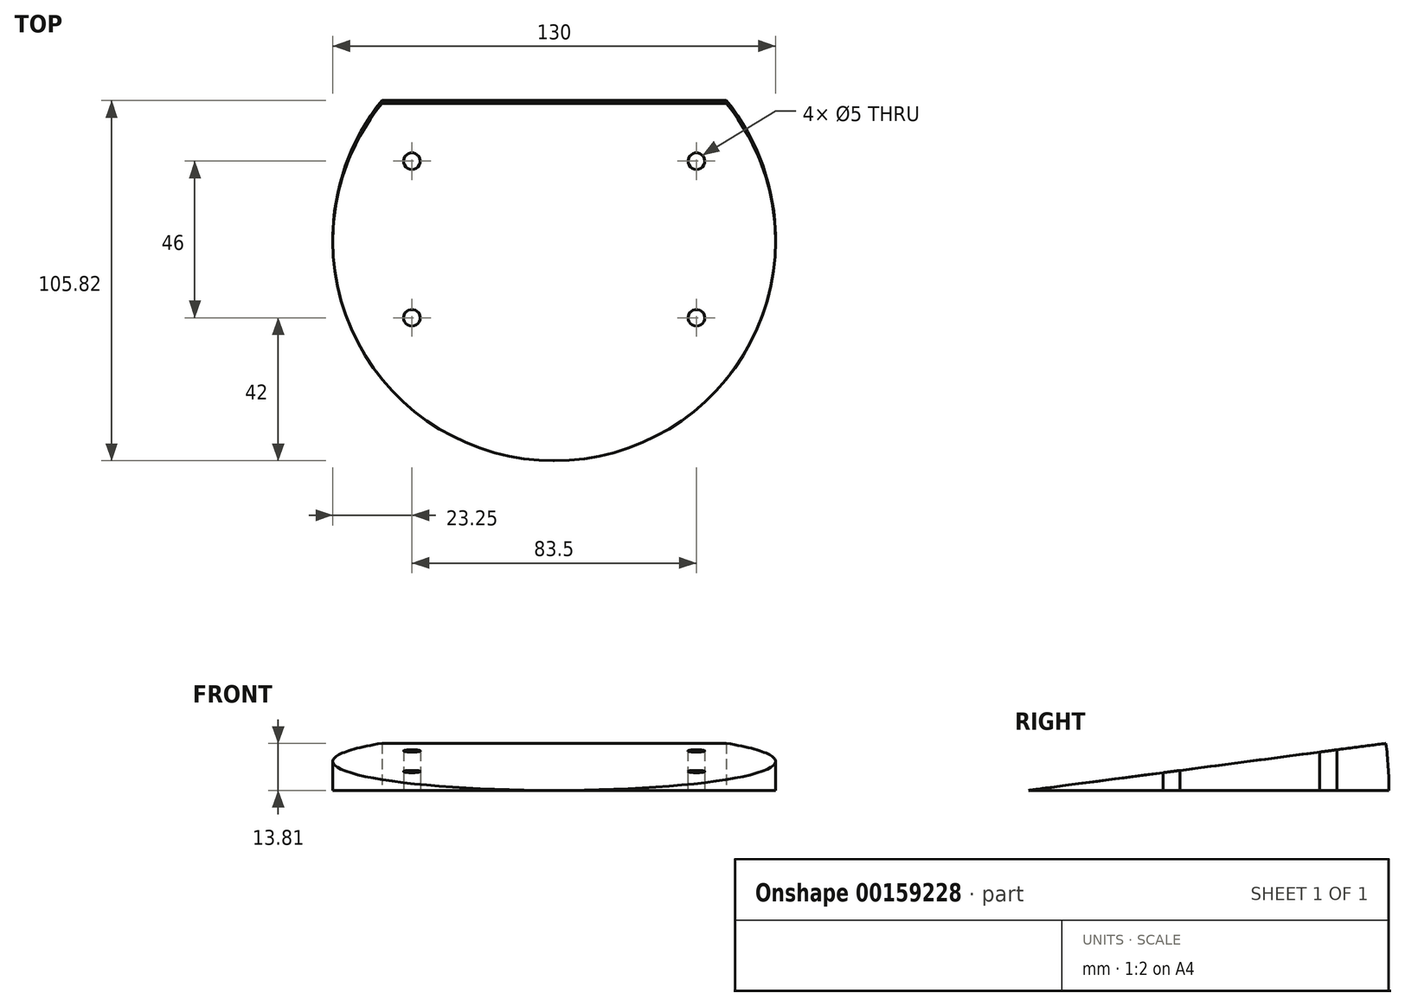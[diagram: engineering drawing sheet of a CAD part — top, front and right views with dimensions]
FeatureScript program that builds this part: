
annotation { "Feature Type Name" : "Feature", "Feature Type Description" : "" }
export const myFeature = defineFeature(function(context is Context, id is Id, definition is map)
    precondition{}
    {
        {
            var Q0;
            Q0=qCreatedBy(makeId("Top.planeOp"),FACE);
            var sketch = newSketch(context, id + "F0", { "sketchPlane" : qUnion([Q0])});
            skCircle(sketch, "E0", {"center": v(0, 0) * mm, "radius": 65 * mm});
            skLineSegment(sketch, "E1.bottom", {"start": v(41.75, -23) * mm, "end": v(-41.75, -23) * mm});
            skLineSegment(sketch, "E1.top", {"start": v(41.75, 23) * mm, "end": v(-41.75, 23) * mm});
            skLineSegment(sketch, "E1.left", {"start": v(41.75, -23) * mm, "end": v(41.75, 23) * mm});
            skLineSegment(sketch, "E1.right", {"start": v(-41.75, -23) * mm, "end": v(-41.75, 23) * mm});
            skCircle(sketch, "E2", {"center": v(-41.75, 23) * mm, "radius": 2.5 * mm});
            skCircle(sketch, "E3.0.1.0", {"center": v(-41.75, -23) * mm, "radius": 2.5 * mm});
            skCircle(sketch, "E3.1.0.0", {"center": v(41.75, 23) * mm, "radius": 2.5 * mm});
            skCircle(sketch, "E3.1.1.0", {"center": v(41.75, -23) * mm, "radius": 2.5 * mm});
            skLineSegment(sketch, "E3.direction1", {"start": v(-41.75, 23) * mm, "end": v(41.75, 23) * mm, "construction": true});
            skLineSegment(sketch, "E3.direction2", {"start": v(-41.75, 23) * mm, "end": v(-41.75, -23) * mm, "construction": true});
            skLineSegment(sketch, "E4", {"start": v(0, -65) * mm, "end": v(66.65, -65) * mm});
            skLineSegment(sketch, "E5", {"start": v(50.59, 40.82) * mm, "end": v(-50.59, 40.82) * mm});
            skSolve(sketch);
        }
        {
            var Q0;
            Q0=makeQuery(id+"F0.imprint","IMPRINT",FACE,{"disambiguationData":[TD([[makeQuery(id+"F0.imprint","IMPRINT",EDGE,{"derivedFrom":sQuery(id+"F0.wireOp",EDGE,"E0")}),1.0]])]});
            var Q1;
            {var subQ5=sQuery(id+"F0.wireOp",EDGE,"E3.1.1.0");var subQ13=sQuery(id+"F0.wireOp",EDGE,"E1.bottom");var subQ14=makeQuery(id+"F0.imprint","INTERSECT",VERTEX,{"derivedFrom":[subQ13,subQ5]});Q1=makeQuery(id+"F0.imprint","IMPRINT",FACE,{"disambiguationData":[TD([[makeQuery(id+"F0.imprint","IMPRINT",EDGE,{"disambiguationData":[TD([[subQ14,-1.0]])],"derivedFrom":subQ13}),-1.0]])]});}
            var Q2;
            {var subQ0=sQuery(id+"F0.wireOp",EDGE,"E1.right");var subQ1=sQuery(id+"F0.wireOp",EDGE,"E1.bottom");var subQ2=makeQuery(id+"F0.imprint","INTERSECT",VERTEX,{"derivedFrom":[subQ1,subQ0]});Q2=makeQuery(id+"F0.imprint","IMPRINT",FACE,{"disambiguationData":[TD([[makeQuery(id+"F0.imprint","IMPRINT",EDGE,{"disambiguationData":[TD([[subQ2,1.0]])],"derivedFrom":subQ1}),1.0]])]});}
            var Q3;
            {var subQ0=sQuery(id+"F0.wireOp",EDGE,"E1.left");var subQ1=sQuery(id+"F0.wireOp",EDGE,"E1.bottom");var subQ2=makeQuery(id+"F0.imprint","INTERSECT",VERTEX,{"derivedFrom":[subQ1,subQ0]});Q3=makeQuery(id+"F0.imprint","IMPRINT",FACE,{"disambiguationData":[TD([[makeQuery(id+"F0.imprint","IMPRINT",EDGE,{"disambiguationData":[TD([[subQ2,-1.0]])],"derivedFrom":subQ1}),1.0]])]});}
            var Q4;
            {var subQ0=sQuery(id+"F0.wireOp",EDGE,"E1.left");var subQ1=sQuery(id+"F0.wireOp",EDGE,"E1.top");var subQ2=makeQuery(id+"F0.imprint","INTERSECT",VERTEX,{"derivedFrom":[subQ1,subQ0]});Q4=makeQuery(id+"F0.imprint","IMPRINT",FACE,{"disambiguationData":[TD([[makeQuery(id+"F0.imprint","IMPRINT",EDGE,{"disambiguationData":[TD([[subQ2,-1.0]])],"derivedFrom":subQ1}),1.0]])]});}
            var Q5;
            {var subQ0=sQuery(id+"F0.wireOp",EDGE,"E1.right");var subQ1=sQuery(id+"F0.wireOp",EDGE,"E1.top");var subQ2=makeQuery(id+"F0.imprint","INTERSECT",VERTEX,{"derivedFrom":[subQ1,subQ0]});Q5=makeQuery(id+"F0.imprint","IMPRINT",FACE,{"disambiguationData":[TD([[makeQuery(id+"F0.imprint","IMPRINT",EDGE,{"disambiguationData":[TD([[subQ2,1.0]])],"derivedFrom":subQ1}),1.0]])]});}
            var Q6;
            {var subQ0=sQuery(id+"F0.wireOp",EDGE,"E1.right");var subQ1=sQuery(id+"F0.wireOp",EDGE,"E1.top");var subQ2=makeQuery(id+"F0.imprint","INTERSECT",VERTEX,{"derivedFrom":[subQ1,subQ0]});Q6=makeQuery(id+"F0.imprint","IMPRINT",FACE,{"disambiguationData":[TD([[makeQuery(id+"F0.imprint","IMPRINT",EDGE,{"disambiguationData":[TD([[subQ2,1.0]])],"derivedFrom":subQ1}),-1.0]])]});}
            var Q7;
            {var subQ0=sQuery(id+"F0.wireOp",EDGE,"E1.right");var subQ1=sQuery(id+"F0.wireOp",EDGE,"E1.bottom");var subQ2=makeQuery(id+"F0.imprint","INTERSECT",VERTEX,{"derivedFrom":[subQ1,subQ0]});Q7=makeQuery(id+"F0.imprint","IMPRINT",FACE,{"disambiguationData":[TD([[makeQuery(id+"F0.imprint","IMPRINT",EDGE,{"disambiguationData":[TD([[subQ2,1.0]])],"derivedFrom":subQ1}),-1.0]])]});}
            var Q8;
            {var subQ0=sQuery(id+"F0.wireOp",EDGE,"E1.left");var subQ1=sQuery(id+"F0.wireOp",EDGE,"E1.bottom");var subQ2=makeQuery(id+"F0.imprint","INTERSECT",VERTEX,{"derivedFrom":[subQ1,subQ0]});Q8=makeQuery(id+"F0.imprint","IMPRINT",FACE,{"disambiguationData":[TD([[makeQuery(id+"F0.imprint","IMPRINT",EDGE,{"disambiguationData":[TD([[subQ2,-1.0]])],"derivedFrom":subQ1}),-1.0]])]});}
            var Q9;
            {var subQ0=sQuery(id+"F0.wireOp",EDGE,"E1.left");var subQ1=sQuery(id+"F0.wireOp",EDGE,"E1.top");var subQ2=makeQuery(id+"F0.imprint","INTERSECT",VERTEX,{"derivedFrom":[subQ1,subQ0]});Q9=makeQuery(id+"F0.imprint","IMPRINT",FACE,{"disambiguationData":[TD([[makeQuery(id+"F0.imprint","IMPRINT",EDGE,{"disambiguationData":[TD([[subQ2,-1.0]])],"derivedFrom":subQ1}),-1.0]])]});}
            var Q10;
            {var subQ0=sQuery(id+"F0.wireOp",EDGE,"61955078-7550-41af-9b48-997e45a96210.0.1.0");var subQ1=sQuery(id+"F0.wireOp",EDGE,"E1.bottom");var subQ2=makeQuery(id+"F0.imprint","INTERSECT",VERTEX,{"derivedFrom":[subQ1,subQ0]});Q10=makeQuery(id+"F0.imprint","IMPRINT",FACE,{"disambiguationData":[TD([[makeQuery(id+"F0.imprint","IMPRINT",EDGE,{"disambiguationData":[TD([[subQ2,-1.0]])],"derivedFrom":subQ1}),-1.0]])]});}
            var Q11;
            {var subQ0=sQuery(id+"F0.wireOp",EDGE,"61955078-7550-41af-9b48-997e45a96210.0.1.0");var subQ1=sQuery(id+"F0.wireOp",EDGE,"E1.bottom");var subQ2=makeQuery(id+"F0.imprint","INTERSECT",VERTEX,{"derivedFrom":[subQ1,subQ0]});Q11=makeQuery(id+"F0.imprint","IMPRINT",FACE,{"disambiguationData":[TD([[makeQuery(id+"F0.imprint","IMPRINT",EDGE,{"disambiguationData":[TD([[subQ2,-1.0]])],"derivedFrom":subQ1}),1.0]])]});}
            var Q12;
            {var subQ0=sQuery(id+"F0.wireOp",EDGE,"61955078-7550-41af-9b48-997e45a96210.1.1.0");var subQ6=sQuery(id+"F0.wireOp",EDGE,"E1.bottom");var subQ15=makeQuery(id+"F0.imprint","INTERSECT",VERTEX,{"derivedFrom":[subQ6,subQ0]});Q12=makeQuery(id+"F0.imprint","IMPRINT",FACE,{"disambiguationData":[TD([[makeQuery(id+"F0.imprint","IMPRINT",EDGE,{"disambiguationData":[TD([[subQ15,-1.0]])],"derivedFrom":subQ6}),-1.0]])]});}
            var Q13;
            {var subQ0=sQuery(id+"F0.wireOp",EDGE,"YlbtFvMg-89HG-Mmdf-bFzC-3wuNxcR9Jd2W");var subQ1=sQuery(id+"F0.wireOp",EDGE,"E1.top");var subQ2=makeQuery(id+"F0.imprint","INTERSECT",VERTEX,{"derivedFrom":[subQ1,subQ0]});Q13=makeQuery(id+"F0.imprint","IMPRINT",FACE,{"disambiguationData":[TD([[makeQuery(id+"F0.imprint","IMPRINT",EDGE,{"disambiguationData":[TD([[subQ2,-1.0]])],"derivedFrom":subQ1}),1.0]])]});}
            var Q14;
            {var subQ0=sQuery(id+"F0.wireOp",EDGE,"YlbtFvMg-89HG-Mmdf-bFzC-3wuNxcR9Jd2W");var subQ1=sQuery(id+"F0.wireOp",EDGE,"E1.top");var subQ2=makeQuery(id+"F0.imprint","INTERSECT",VERTEX,{"derivedFrom":[subQ1,subQ0]});Q14=makeQuery(id+"F0.imprint","IMPRINT",FACE,{"disambiguationData":[TD([[makeQuery(id+"F0.imprint","IMPRINT",EDGE,{"disambiguationData":[TD([[subQ2,-1.0]])],"derivedFrom":subQ1}),-1.0]])]});}
            var Q15;
            {var subQ0=sQuery(id+"F0.wireOp",EDGE,"E3.1.0.0");var subQ1=sQuery(id+"F0.wireOp",EDGE,"E1.top");var subQ2=makeQuery(id+"F0.imprint","INTERSECT",VERTEX,{"derivedFrom":[subQ1,subQ0]});Q15=makeQuery(id+"F0.imprint","IMPRINT",FACE,{"disambiguationData":[TD([[makeQuery(id+"F0.imprint","IMPRINT",EDGE,{"disambiguationData":[TD([[subQ2,-1.0]])],"derivedFrom":subQ1}),1.0]])]});}
            var Q16;
            {var subQ0=sQuery(id+"F0.wireOp",EDGE,"E3.1.0.0");var subQ1=sQuery(id+"F0.wireOp",EDGE,"E1.top");var subQ2=makeQuery(id+"F0.imprint","INTERSECT",VERTEX,{"derivedFrom":[subQ1,subQ0]});Q16=makeQuery(id+"F0.imprint","IMPRINT",FACE,{"disambiguationData":[TD([[makeQuery(id+"F0.imprint","IMPRINT",EDGE,{"disambiguationData":[TD([[subQ2,-1.0]])],"derivedFrom":subQ1}),-1.0]])]});}
            var Q17;
            {var subQ0=sQuery(id+"F0.wireOp",EDGE,"E3.1.1.0");var subQ1=sQuery(id+"F0.wireOp",EDGE,"E1.bottom");var subQ2=makeQuery(id+"F0.imprint","INTERSECT",VERTEX,{"derivedFrom":[subQ1,subQ0]});Q17=makeQuery(id+"F0.imprint","IMPRINT",FACE,{"disambiguationData":[TD([[makeQuery(id+"F0.imprint","IMPRINT",EDGE,{"disambiguationData":[TD([[subQ2,-1.0]])],"derivedFrom":subQ1}),1.0]])]});}
            var Q18;
            {var subQ0=sQuery(id+"F0.wireOp",EDGE,"61955078-7550-41af-9b48-997e45a96210.1.0.0");var subQ1=sQuery(id+"F0.wireOp",EDGE,"E1.top");var subQ2=makeQuery(id+"F0.imprint","INTERSECT",VERTEX,{"derivedFrom":[subQ1,subQ0]});Q18=makeQuery(id+"F0.imprint","IMPRINT",FACE,{"disambiguationData":[TD([[makeQuery(id+"F0.imprint","IMPRINT",EDGE,{"disambiguationData":[TD([[subQ2,-1.0]])],"derivedFrom":subQ1}),-1.0]])]});}
            var Q19;
            {var subQ0=sQuery(id+"F0.wireOp",EDGE,"6T6w9VIw-9FXo-ThLn-9DWL-4RXQOPPDTeL3.top");var subQ1=sQuery(id+"F0.wireOp",EDGE,"61955078-7550-41af-9b48-997e45a96210.1.0.0");var subQ2=makeQuery(id+"F0.imprint","INTERSECT",VERTEX,{"derivedFrom":[subQ1,subQ0]});Q19=makeQuery(id+"F0.imprint","IMPRINT",FACE,{"disambiguationData":[TD([[makeQuery(id+"F0.imprint","IMPRINT",EDGE,{"disambiguationData":[TD([[subQ2,1.0]])],"derivedFrom":subQ1}),1.0]])]});}
            var Q20;
            {var subQ0=sQuery(id+"F0.wireOp",EDGE,"61955078-7550-41af-9b48-997e45a96210.1.1.0");var subQ1=sQuery(id+"F0.wireOp",EDGE,"E1.left");var subQ2=makeQuery(id+"F0.imprint","INTERSECT",VERTEX,{"derivedFrom":[subQ1,subQ0]});Q20=makeQuery(id+"F0.imprint","IMPRINT",FACE,{"disambiguationData":[TD([[makeQuery(id+"F0.imprint","IMPRINT",EDGE,{"disambiguationData":[TD([[subQ2,-1.0]])],"derivedFrom":subQ1}),-1.0]])]});}
            var Q21;
            {var subQ0=sQuery(id+"F0.wireOp",EDGE,"6T6w9VIw-9FXo-ThLn-9DWL-4RXQOPPDTeL3.left");var subQ1=sQuery(id+"F0.wireOp",EDGE,"61955078-7550-41af-9b48-997e45a96210.1.1.0");var subQ2=makeQuery(id+"F0.imprint","INTERSECT",VERTEX,{"derivedFrom":[subQ1,subQ0]});Q21=makeQuery(id+"F0.imprint","IMPRINT",FACE,{"disambiguationData":[TD([[makeQuery(id+"F0.imprint","IMPRINT",EDGE,{"disambiguationData":[TD([[subQ2,1.0]])],"derivedFrom":subQ1}),1.0]])]});}
            var Q22;
            {var subQ0=sQuery(id+"F0.wireOp",EDGE,"61955078-7550-41af-9b48-997e45a96210.1.1.0");var subQ1=sQuery(id+"F0.wireOp",EDGE,"E1.bottom");var subQ2=makeQuery(id+"F0.imprint","INTERSECT",VERTEX,{"derivedFrom":[subQ1,subQ0]});Q22=makeQuery(id+"F0.imprint","IMPRINT",FACE,{"disambiguationData":[TD([[makeQuery(id+"F0.imprint","IMPRINT",EDGE,{"disambiguationData":[TD([[subQ2,-1.0]])],"derivedFrom":subQ1}),1.0]])]});}
            var Q23;
            {var subQ0=sQuery(id+"F0.wireOp",EDGE,"61955078-7550-41af-9b48-997e45a96210.0.1.0");var subQ1=sQuery(id+"F0.wireOp",EDGE,"E1.right");var subQ2=makeQuery(id+"F0.imprint","INTERSECT",VERTEX,{"derivedFrom":[subQ1,subQ0]});Q23=makeQuery(id+"F0.imprint","IMPRINT",FACE,{"disambiguationData":[TD([[makeQuery(id+"F0.imprint","IMPRINT",EDGE,{"disambiguationData":[TD([[subQ2,-1.0]])],"derivedFrom":subQ1}),1.0]])]});}
            var Q24;
            {var subQ0=sQuery(id+"F0.wireOp",EDGE,"6T6w9VIw-9FXo-ThLn-9DWL-4RXQOPPDTeL3.right");var subQ1=sQuery(id+"F0.wireOp",EDGE,"61955078-7550-41af-9b48-997e45a96210.0.1.0");var subQ2=makeQuery(id+"F0.imprint","INTERSECT",VERTEX,{"derivedFrom":[subQ1,subQ0]});Q24=makeQuery(id+"F0.imprint","IMPRINT",FACE,{"disambiguationData":[TD([[makeQuery(id+"F0.imprint","IMPRINT",EDGE,{"disambiguationData":[TD([[subQ2,-1.0]])],"derivedFrom":subQ1}),1.0]])]});}
            var Q25;
            {var subQ0=sQuery(id+"F0.wireOp",EDGE,"6T6w9VIw-9FXo-ThLn-9DWL-4RXQOPPDTeL3.top");var subQ1=sQuery(id+"F0.wireOp",EDGE,"YlbtFvMg-89HG-Mmdf-bFzC-3wuNxcR9Jd2W");var subQ2=makeQuery(id+"F0.imprint","INTERSECT",VERTEX,{"derivedFrom":[subQ1,subQ0]});Q25=makeQuery(id+"F0.imprint","IMPRINT",FACE,{"disambiguationData":[TD([[makeQuery(id+"F0.imprint","IMPRINT",EDGE,{"disambiguationData":[TD([[subQ2,-1.0]])],"derivedFrom":subQ1}),1.0]])]});}
            var Q26;
            Q26=sQuery(id+"F0.wireOp",EDGE,"E4");
            revolve(context, id + "F1", {"entities" : qUnion([Q0, Q1, Q2, Q3, Q4, Q5, Q6, Q7, Q8, Q9, Q10, Q11, Q12, Q13, Q14, Q15, Q16, Q17, Q18, Q19, Q20, Q21, Q22, Q23, Q24, Q25]), "axis" : qUnion([Q26]), "revolveType" : RevolveType.ONE_DIRECTION, "angle" : 7.5 * degree});
        }
        {
            var Q0;
            {var subQ0=sQuery(id+"F0.wireOp",EDGE,"E1.right");var subQ1=sQuery(id+"F0.wireOp",EDGE,"E1.bottom");var subQ2=makeQuery(id+"F0.imprint","INTERSECT",VERTEX,{"derivedFrom":[subQ1,subQ0]});Q0=makeQuery(id+"F0.imprint","IMPRINT",FACE,{"disambiguationData":[TD([[makeQuery(id+"F0.imprint","IMPRINT",EDGE,{"disambiguationData":[TD([[subQ2,1.0]])],"derivedFrom":subQ1}),-1.0]])]});}
            var Q1;
            {var subQ0=sQuery(id+"F0.wireOp",EDGE,"E1.right");var subQ1=sQuery(id+"F0.wireOp",EDGE,"E1.bottom");var subQ2=makeQuery(id+"F0.imprint","INTERSECT",VERTEX,{"derivedFrom":[subQ1,subQ0]});Q1=makeQuery(id+"F0.imprint","IMPRINT",FACE,{"disambiguationData":[TD([[makeQuery(id+"F0.imprint","IMPRINT",EDGE,{"disambiguationData":[TD([[subQ2,1.0]])],"derivedFrom":subQ1}),1.0]])]});}
            var Q2;
            {var subQ0=sQuery(id+"F0.wireOp",EDGE,"E1.left");var subQ1=sQuery(id+"F0.wireOp",EDGE,"E1.bottom");var subQ2=makeQuery(id+"F0.imprint","INTERSECT",VERTEX,{"derivedFrom":[subQ1,subQ0]});Q2=makeQuery(id+"F0.imprint","IMPRINT",FACE,{"disambiguationData":[TD([[makeQuery(id+"F0.imprint","IMPRINT",EDGE,{"disambiguationData":[TD([[subQ2,-1.0]])],"derivedFrom":subQ1}),-1.0]])]});}
            var Q3;
            {var subQ0=sQuery(id+"F0.wireOp",EDGE,"E1.left");var subQ1=sQuery(id+"F0.wireOp",EDGE,"E1.bottom");var subQ2=makeQuery(id+"F0.imprint","INTERSECT",VERTEX,{"derivedFrom":[subQ1,subQ0]});Q3=makeQuery(id+"F0.imprint","IMPRINT",FACE,{"disambiguationData":[TD([[makeQuery(id+"F0.imprint","IMPRINT",EDGE,{"disambiguationData":[TD([[subQ2,-1.0]])],"derivedFrom":subQ1}),1.0]])]});}
            var Q4;
            {var subQ0=sQuery(id+"F0.wireOp",EDGE,"E1.left");var subQ1=sQuery(id+"F0.wireOp",EDGE,"E1.top");var subQ2=makeQuery(id+"F0.imprint","INTERSECT",VERTEX,{"derivedFrom":[subQ1,subQ0]});Q4=makeQuery(id+"F0.imprint","IMPRINT",FACE,{"disambiguationData":[TD([[makeQuery(id+"F0.imprint","IMPRINT",EDGE,{"disambiguationData":[TD([[subQ2,-1.0]])],"derivedFrom":subQ1}),1.0]])]});}
            var Q5;
            {var subQ0=sQuery(id+"F0.wireOp",EDGE,"E1.left");var subQ1=sQuery(id+"F0.wireOp",EDGE,"E1.top");var subQ2=makeQuery(id+"F0.imprint","INTERSECT",VERTEX,{"derivedFrom":[subQ1,subQ0]});Q5=makeQuery(id+"F0.imprint","IMPRINT",FACE,{"disambiguationData":[TD([[makeQuery(id+"F0.imprint","IMPRINT",EDGE,{"disambiguationData":[TD([[subQ2,-1.0]])],"derivedFrom":subQ1}),-1.0]])]});}
            var Q6;
            {var subQ0=sQuery(id+"F0.wireOp",EDGE,"E1.right");var subQ1=sQuery(id+"F0.wireOp",EDGE,"E1.top");var subQ2=makeQuery(id+"F0.imprint","INTERSECT",VERTEX,{"derivedFrom":[subQ1,subQ0]});Q6=makeQuery(id+"F0.imprint","IMPRINT",FACE,{"disambiguationData":[TD([[makeQuery(id+"F0.imprint","IMPRINT",EDGE,{"disambiguationData":[TD([[subQ2,1.0]])],"derivedFrom":subQ1}),1.0]])]});}
            var Q7;
            {var subQ0=sQuery(id+"F0.wireOp",EDGE,"E1.right");var subQ1=sQuery(id+"F0.wireOp",EDGE,"E1.top");var subQ2=makeQuery(id+"F0.imprint","INTERSECT",VERTEX,{"derivedFrom":[subQ1,subQ0]});Q7=makeQuery(id+"F0.imprint","IMPRINT",FACE,{"disambiguationData":[TD([[makeQuery(id+"F0.imprint","IMPRINT",EDGE,{"disambiguationData":[TD([[subQ2,1.0]])],"derivedFrom":subQ1}),-1.0]])]});}
            extrude(context, id + "F2", {"entities" : qUnion([Q0, Q1, Q2, Q3, Q4, Q5, Q6, Q7]), "operationType" : NewBodyOperationType.REMOVE, "endBound" : BoundingType.THROUGH_ALL, "depth" : 25 * mm});
        }
    });
